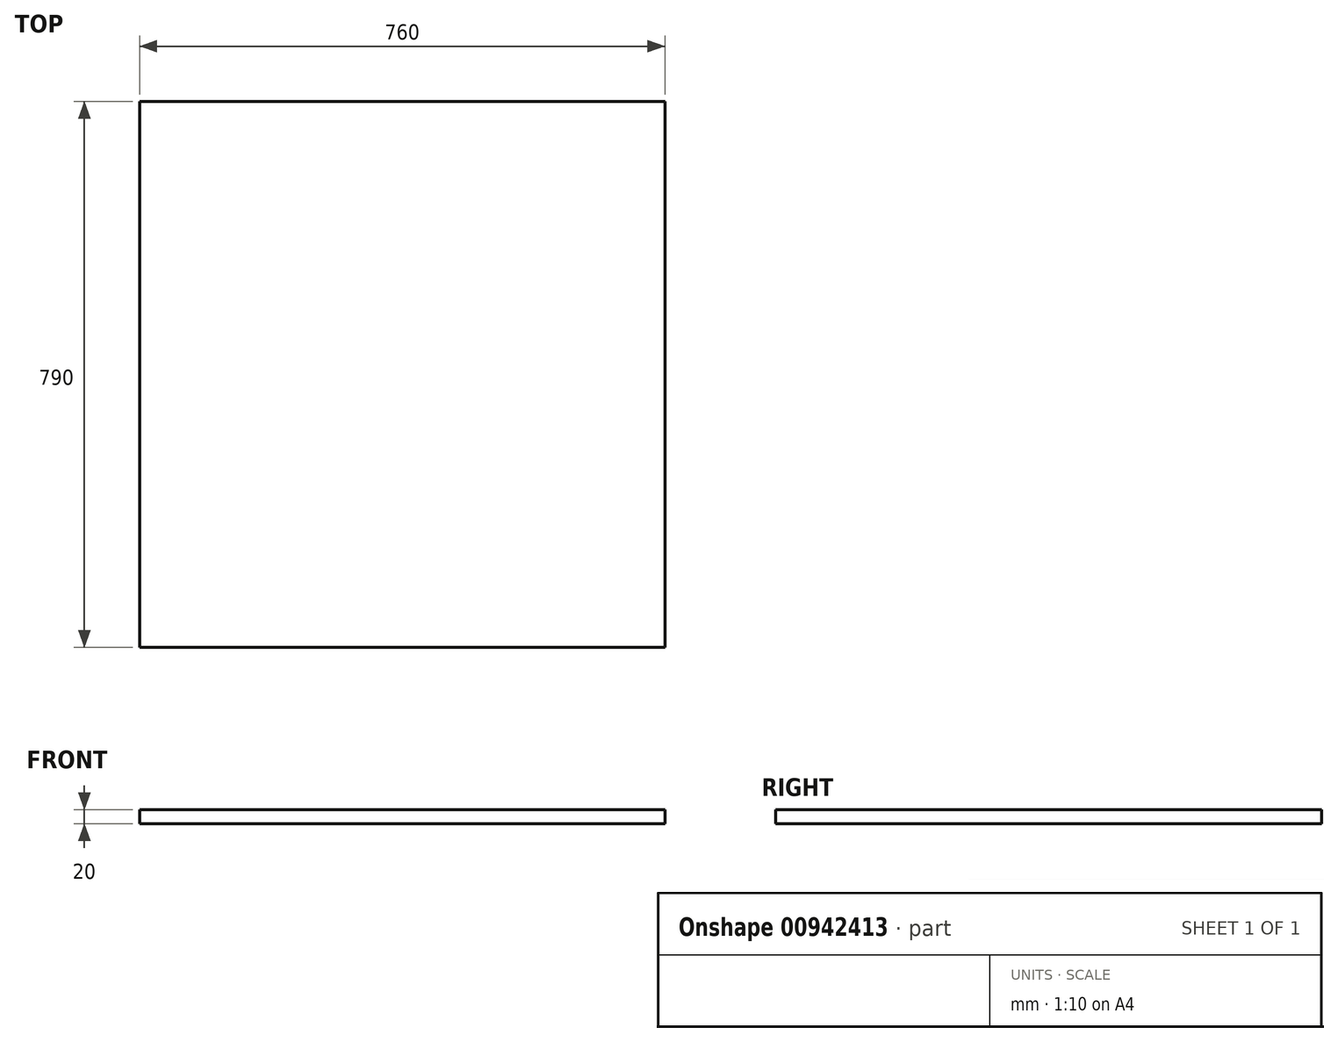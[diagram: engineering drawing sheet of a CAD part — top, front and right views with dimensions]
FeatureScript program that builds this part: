
annotation { "Feature Type Name" : "Feature", "Feature Type Description" : "" }
export const myFeature = defineFeature(function(context is Context, id is Id, definition is map)
    precondition{}
    {
        {
            var Q0;
            Q0=qCreatedBy(makeId("Top.planeOp"),FACE);
            var sketch = newSketch(context, id + "F0", { "sketchPlane" : qUnion([Q0])});
            skLineSegment(sketch, "E0.bottom", {"start": v(0, 0) * mm, "end": v(760, 0) * mm});
            skLineSegment(sketch, "E0.top", {"start": v(0, 790) * mm, "end": v(760, 790) * mm});
            skLineSegment(sketch, "E0.left", {"start": v(0, 0) * mm, "end": v(0, 790) * mm});
            skLineSegment(sketch, "E0.right", {"start": v(760, 0) * mm, "end": v(760, 790) * mm});
            skSolve(sketch);
        }
        {
            var Q0;
            Q0 = qSketchRegion(id + "F0", true);
            extrude(context, id + "F1", {"entities" : qUnion([Q0]), "depth" : 20 * mm, "offsetDistance" : 25 * mm});
        }
    });
